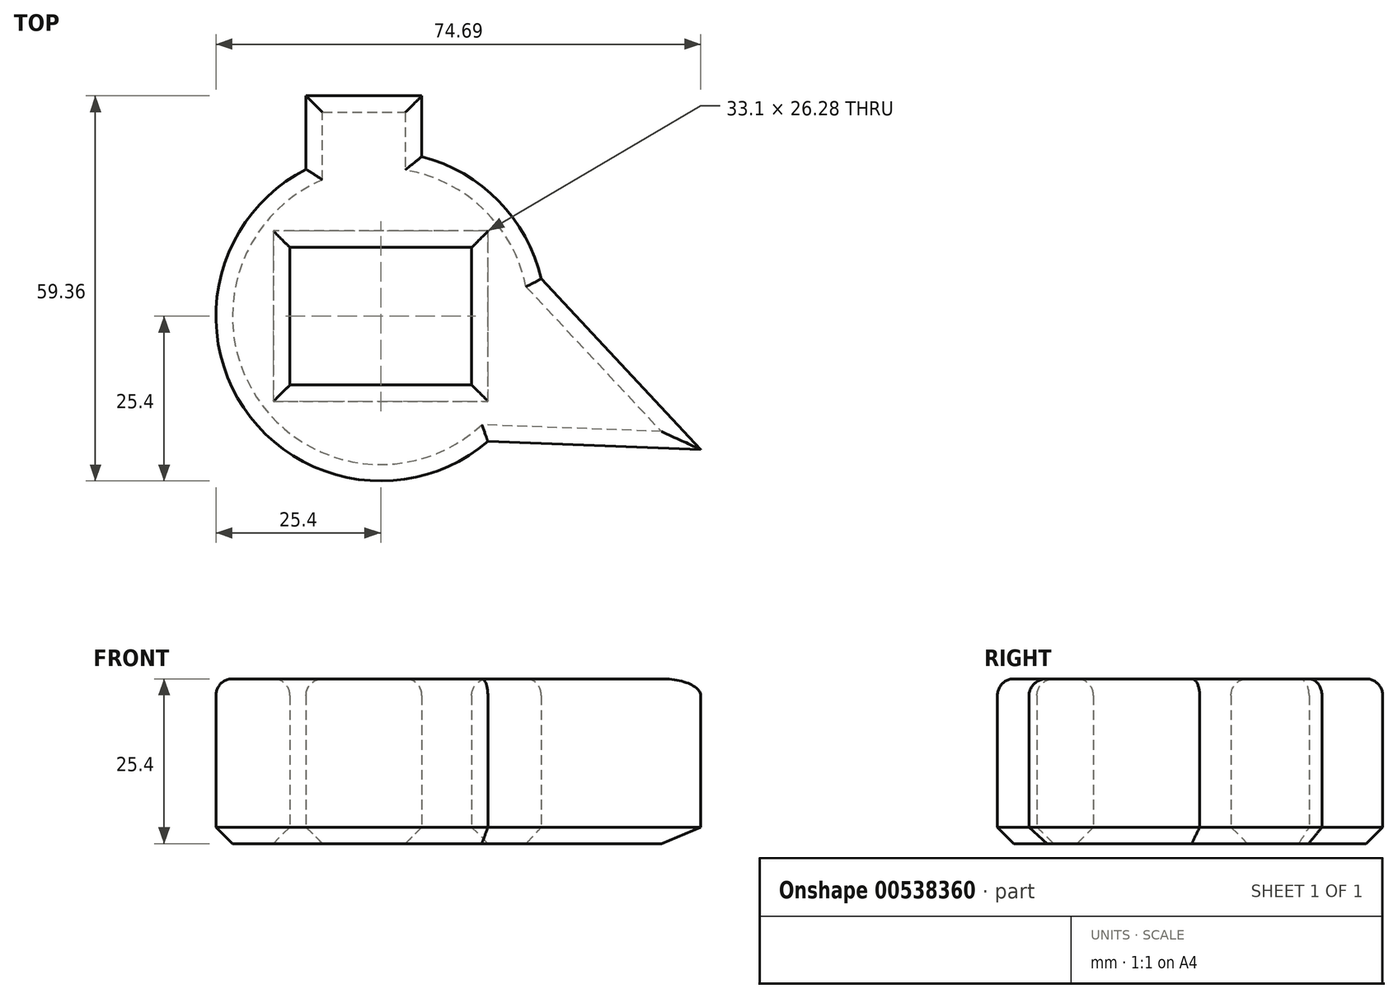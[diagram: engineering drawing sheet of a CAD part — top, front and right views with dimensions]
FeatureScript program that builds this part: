
annotation { "Feature Type Name" : "Feature", "Feature Type Description" : "" }
export const myFeature = defineFeature(function(context is Context, id is Id, definition is map)
    precondition{}
    {
        {
            var Q0;
            Q0=qCreatedBy(makeId("Top.planeOp"),FACE);
            var sketch = newSketch(context, id + "F0", { "sketchPlane" : qUnion([Q0])});
            skArc(sketch, "E0", {"start": v(-11.51, 22.64) * mm, "mid": v(-21.12, -14.1) * mm, "end": v(16.5, -19.3) * mm});
            skLineSegment(sketch, "E1.bottom", {"start": v(-11.51, 33.96) * mm, "end": v(6.33, 33.96) * mm});
            skLineSegment(sketch, "E1.left", {"start": v(-11.51, 33.96) * mm, "end": v(-11.51, 22.64) * mm});
            skLineSegment(sketch, "E2", {"start": v(6.33, 33.96) * mm, "end": v(6.33, 24.6) * mm});
            skLineSegment(sketch, "E3", {"start": v(24.74, 5.77) * mm, "end": v(49.29, -20.53) * mm});
            skLineSegment(sketch, "E4", {"start": v(49.29, -20.53) * mm, "end": v(16.5, -19.3) * mm});
            skArc(sketch, "E5.trimOffspring", {"start": v(24.74, 5.77) * mm, "mid": v(18.16, 17.75) * mm, "end": v(6.33, 24.6) * mm});
            skLineSegment(sketch, "E6.bottom", {"start": v(14.01, 10.6) * mm, "end": v(-14.01, 10.6) * mm});
            skLineSegment(sketch, "E6.top", {"start": v(14.01, -10.6) * mm, "end": v(-14.01, -10.6) * mm});
            skLineSegment(sketch, "E6.left", {"start": v(14.01, 10.6) * mm, "end": v(14.01, -10.6) * mm});
            skLineSegment(sketch, "E6.right", {"start": v(-14.01, 10.6) * mm, "end": v(-14.01, -10.6) * mm});
            skSolve(sketch);
        }
        {
            var Q0;
            Q0 = qSketchRegion(id + "F0", true);
            extrude(context, id + "F1", {"entities" : qUnion([Q0]), "depth" : 25.4 * mm, "offsetDistance" : 25.4 * mm});
        }
        {
            var Q0;
            Q0=makeQuery(id+"F1.opExtrude","CAP_FACE",FACE,{"disambiguationData":[OSD([sQuery(id+"F0.wireOp",EDGE,"E0"),sQuery(id+"F0.wireOp",EDGE,"E1.bottom"),sQuery(id+"F0.wireOp",EDGE,"E1.left"),sQuery(id+"F0.wireOp",EDGE,"E2"),sQuery(id+"F0.wireOp",EDGE,"E3"),sQuery(id+"F0.wireOp",EDGE,"E4"),sQuery(id+"F0.wireOp",EDGE,"E5.trimOffspring"),sQuery(id+"F0.wireOp",EDGE,"E6.bottom"),sQuery(id+"F0.wireOp",EDGE,"E6.top"),sQuery(id+"F0.wireOp",EDGE,"E6.left"),sQuery(id+"F0.wireOp",EDGE,"E6.right")])],"isStart":false});
            fillet(context, id + "F2", {"entities" : qUnion([Q0]), "radius" : 2.54 * mm, "tangentPropagation" : true, "allowEdgeOverflow" : false});
        }
        {
            var Q0;
            Q0=makeQuery(id+"F1.opExtrude","CAP_FACE",FACE,{"disambiguationData":[OSD([sQuery(id+"F0.wireOp",EDGE,"E0"),sQuery(id+"F0.wireOp",EDGE,"E1.bottom"),sQuery(id+"F0.wireOp",EDGE,"E1.left"),sQuery(id+"F0.wireOp",EDGE,"E2"),sQuery(id+"F0.wireOp",EDGE,"E3"),sQuery(id+"F0.wireOp",EDGE,"E4"),sQuery(id+"F0.wireOp",EDGE,"E5.trimOffspring"),sQuery(id+"F0.wireOp",EDGE,"E6.bottom"),sQuery(id+"F0.wireOp",EDGE,"E6.top"),sQuery(id+"F0.wireOp",EDGE,"E6.left"),sQuery(id+"F0.wireOp",EDGE,"E6.right")])],"isStart":true});
            chamfer(context, id + "F3", {"entities" : qUnion([Q0]), "width" : 2.54 * mm, "tangentPropagation" : true});
        }
    });
